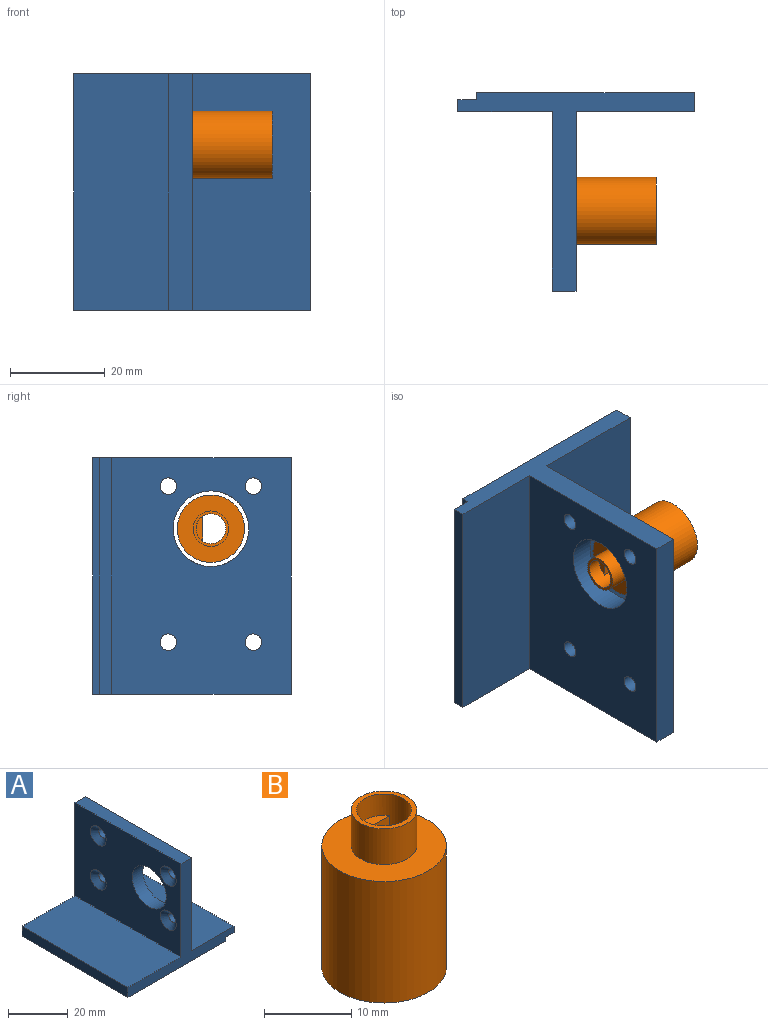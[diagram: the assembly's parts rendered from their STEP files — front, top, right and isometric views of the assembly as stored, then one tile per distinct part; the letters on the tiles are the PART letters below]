
ASSEMBLY  parts=2 mates=1
PART A: 21 faces, bbox 50x50x42 mm
  f0: plane 50x38mm, normal (1,0,0), area 1660.5mm2, adj f2,f3,f8,f9,f12,f13,f14,f15
  f1: plane 50x38mm, normal (-1,0,0), area 1522.2mm2, adj f2,f3,f6,f9,f12,f17,f18,f19
  f2: plane 50x42mm, normal (0,-1,0), area 384mm2, adj f0,f1,f3,f4,f5,f6,f7,f8
  f3: plane 50x5mm, normal (0,0,1), area 250mm2, adj f0,f1,f2,f12
  f4: plane 50x46mm, normal (0,0,-1), area 2300mm2, adj f2,f5,f10,f12
  f5: plane 50x4mm, normal (-1,0,0), area 200mm2, adj f2,f4,f6,f12
  f6: plane 50x25mm, normal (0,0,1), area 1250mm2, adj f1,f2,f5,f12
  f7: plane 50x2.5mm, normal (1,0,0), area 125mm2, adj f2,f8,f11,f12
  f8: plane 50x20mm, normal (0,0,1), area 1000mm2, adj f0,f2,f7,f12
  f9: cylinder r=8mm len=16mm, axis (-1,0,0), area 251.3mm2, adj f0,f1
  f10: plane 50x1.5mm, normal (1,0,0), area 75mm2, adj f2,f4,f11,f12
  f11: plane 50x4mm, normal (0,0,-1), area 200mm2, adj f2,f7,f10,f12
  f12: plane 50x42mm, normal (0,1,0), area 384mm2, adj f0,f1,f3,f4,f5,f6,f7,f8
  f13: cylinder r=1.75mm len=3.5mm, axis (1,0,0), area 33mm2, adj f0,f19
  f14: cylinder r=1.75mm len=3.5mm, axis (1,0,0), area 33mm2, adj f0,f18
  f15: cylinder r=1.75mm len=3.5mm, axis (1,0,0), area 33mm2, adj f0,f20
  f16: cylinder r=1.75mm len=3.5mm, axis (1,0,0), area 33mm2, adj f0,f17
  f17: cone r=3.75mm half-angle=45deg, axis (-1,0,0), area 48.9mm2, adj f1,f16
  f18: cone r=3.75mm half-angle=45deg, axis (-1,0,0), area 48.9mm2, adj f1,f14
  f19: cone r=3.75mm half-angle=45deg, axis (-1,0,0), area 48.9mm2, adj f1,f13
  f20: cone r=3.75mm half-angle=45deg, axis (-1,0,0), area 48.9mm2, adj f1,f15
PART B: 10 faces, bbox 14.3x14.3x22 mm
  f0: cylinder r=3.75mm len=7.5mm, axis (0,0,1), area 47.1mm2, adj f2,f9
  f1: cylinder r=7.12mm len=17mm, axis (0,0,1), area 761.1mm2, adj f2,f3
  f2: plane 14.25x14.25mm, normal (0,0,-1), area 115.3mm2, adj f0,f1
  f3: plane 14.25x14.25mm, normal (0,0,1), area 115.3mm2, adj f1,f5
  f4: cylinder r=3.15mm len=20mm, axis (0,0,-1), area 290.7mm2, adj f6,f7,f8,f9
  f5: cylinder r=3.75mm len=7.5mm, axis (0,0,-1), area 117.8mm2, adj f3,f6
  f6: plane 7.5x7.5mm, normal (0,0,1), area 13mm2, adj f4,f5
  f7: plane 17x5.24mm, normal (0,-1,0), area 89.1mm2, adj f4,f8,f9
  f8: plane 5.24x1.4mm, normal (0,0,1), area 5.2mm2, adj f4,f7
  f9: plane 7.5x7.5mm, normal (0,0,-1), area 18.2mm2, adj f0,f4,f7
PLACE A rot(axis=(0,0.71,-0.71),180deg) t=(6.96,10.32,16.49)mm
PLACE B rot(axis=(0,-1,0),90deg) t=(11.96,-14.68,16.49)mm
MATE revolute A.f9 <-> B.f1  axis (1,0,0) through (6.96,-14.68,16.49)mm
